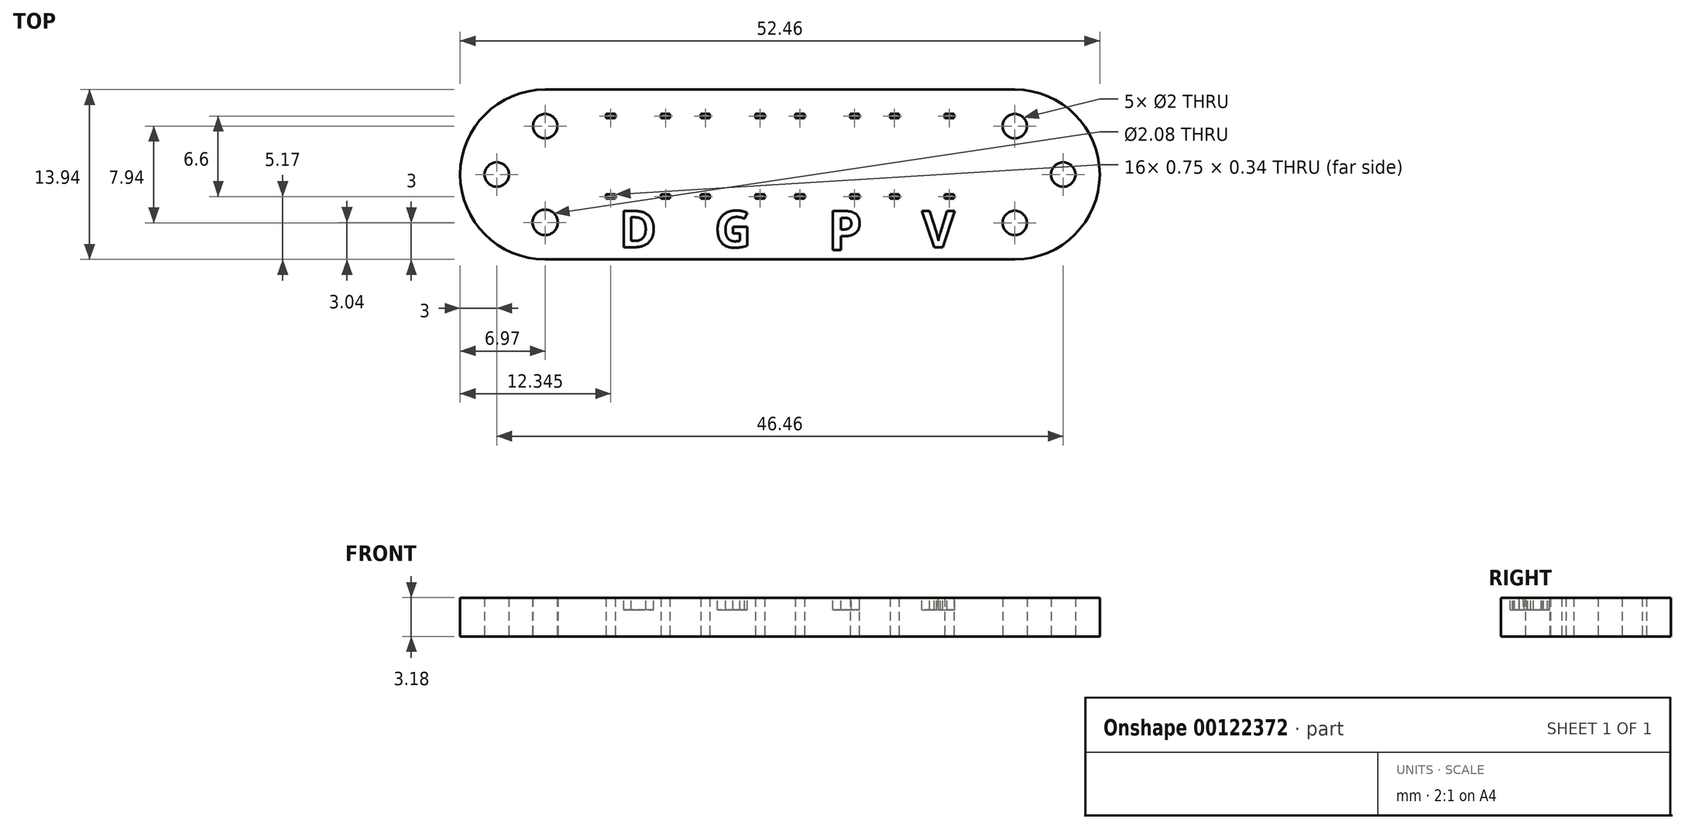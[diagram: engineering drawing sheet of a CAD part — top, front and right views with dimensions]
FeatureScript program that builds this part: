
annotation { "Feature Type Name" : "Feature", "Feature Type Description" : "" }
export const myFeature = defineFeature(function(context is Context, id is Id, definition is map)
    precondition{}
    {
        {
            var Q0;
            Q0=qCreatedBy(makeId("Top.planeOp"),FACE);
            var sketch = newSketch(context, id + "F0", { "sketchPlane" : qUnion([Q0])});
            skLineSegment(sketch, "E0.bottom", {"start": v(0, 0) * mm, "end": v(0.75, 0) * mm});
            skLineSegment(sketch, "E0.top", {"start": v(0, 0.34) * mm, "end": v(0.75, 0.34) * mm});
            skLineSegment(sketch, "E0.left", {"start": v(0, 0) * mm, "end": v(0, 0.34) * mm});
            skLineSegment(sketch, "E0.right", {"start": v(0.75, 0) * mm, "end": v(0.75, 0.34) * mm});
            skLineSegment(sketch, "E1.bottom", {"start": v(4.5, 0) * mm, "end": v(5.24, 0) * mm});
            skLineSegment(sketch, "E1.top", {"start": v(4.5, 0.34) * mm, "end": v(5.24, 0.34) * mm});
            skLineSegment(sketch, "E1.left", {"start": v(4.5, 0) * mm, "end": v(4.5, 0.34) * mm});
            skLineSegment(sketch, "E1.right", {"start": v(5.24, 0) * mm, "end": v(5.24, 0.34) * mm});
            skLineSegment(sketch, "E2.bottom", {"start": v(0, 6.94) * mm, "end": v(0.75, 6.94) * mm});
            skLineSegment(sketch, "E2.top", {"start": v(0, 6.6) * mm, "end": v(0.75, 6.6) * mm});
            skLineSegment(sketch, "E2.left", {"start": v(0, 6.94) * mm, "end": v(0, 6.6) * mm});
            skLineSegment(sketch, "E2.right", {"start": v(0.75, 6.94) * mm, "end": v(0.75, 6.6) * mm});
            skLineSegment(sketch, "E3.bottom", {"start": v(5.24, 6.94) * mm, "end": v(4.5, 6.94) * mm});
            skLineSegment(sketch, "E3.top", {"start": v(5.24, 6.6) * mm, "end": v(4.5, 6.6) * mm});
            skLineSegment(sketch, "E3.left", {"start": v(5.24, 6.94) * mm, "end": v(5.24, 6.6) * mm});
            skLineSegment(sketch, "E3.right", {"start": v(4.5, 6.94) * mm, "end": v(4.5, 6.6) * mm});
            skLineSegment(sketch, "E4", {"start": v(6.5, 0) * mm, "end": v(6.5, 8) * mm});
            skLineSegment(sketch, "E5.MirrorCS", {"start": v(7.76, 0) * mm, "end": v(7.76, 0.34) * mm});
            skLineSegment(sketch, "E6.MirrorCS", {"start": v(13, 6.94) * mm, "end": v(13, 6.6) * mm});
            skLineSegment(sketch, "E7.MirrorCS", {"start": v(12.25, 6.94) * mm, "end": v(12.25, 6.6) * mm});
            skLineSegment(sketch, "E8.MirrorCS", {"start": v(7.76, 6.94) * mm, "end": v(7.76, 6.6) * mm});
            skLineSegment(sketch, "E9.MirrorCS", {"start": v(8.5, 6.94) * mm, "end": v(8.5, 6.6) * mm});
            skLineSegment(sketch, "E10.MirrorCS", {"start": v(8.5, 0) * mm, "end": v(8.5, 0.34) * mm});
            skLineSegment(sketch, "E11.MirrorCS", {"start": v(13, 0) * mm, "end": v(13, 0.34) * mm});
            skLineSegment(sketch, "E12.MirrorCS", {"start": v(12.25, 0) * mm, "end": v(12.25, 0.34) * mm});
            skLineSegment(sketch, "E13.MirrorCS", {"start": v(13, 6.6) * mm, "end": v(12.25, 6.6) * mm});
            skLineSegment(sketch, "E14.MirrorCS", {"start": v(13, 6.94) * mm, "end": v(12.25, 6.94) * mm});
            skLineSegment(sketch, "E15.MirrorCS", {"start": v(7.76, 6.94) * mm, "end": v(8.5, 6.94) * mm});
            skLineSegment(sketch, "E16.MirrorCS", {"start": v(13, 0) * mm, "end": v(12.25, 0) * mm});
            skLineSegment(sketch, "E17.MirrorCS", {"start": v(13, 0.34) * mm, "end": v(12.25, 0.34) * mm});
            skLineSegment(sketch, "E18.MirrorCS", {"start": v(7.76, 6.6) * mm, "end": v(8.5, 6.6) * mm});
            skLineSegment(sketch, "E19.MirrorCS", {"start": v(8.5, 0) * mm, "end": v(7.76, 0) * mm});
            skLineSegment(sketch, "E20.MirrorCS", {"start": v(8.5, 0.34) * mm, "end": v(7.76, 0.34) * mm});
            skLineSegment(sketch, "E21", {"start": v(14.26, 0) * mm, "end": v(14.26, 8) * mm});
            skLineSegment(sketch, "E22.MirrorCS", {"start": v(15.52, 6.94) * mm, "end": v(15.52, 6.6) * mm});
            skLineSegment(sketch, "E23.MirrorCS", {"start": v(20.01, 0) * mm, "end": v(20.01, 0.34) * mm});
            skLineSegment(sketch, "E24.MirrorCS", {"start": v(20.76, 0) * mm, "end": v(20.76, 0.34) * mm});
            skLineSegment(sketch, "E25.MirrorCS", {"start": v(20.01, 6.94) * mm, "end": v(20.01, 6.6) * mm});
            skLineSegment(sketch, "E26.MirrorCS", {"start": v(16.27, 0) * mm, "end": v(16.27, 0.34) * mm});
            skLineSegment(sketch, "E27.MirrorCS", {"start": v(20.76, 6.94) * mm, "end": v(20.76, 6.6) * mm});
            skLineSegment(sketch, "E28.MirrorCS", {"start": v(16.27, 6.94) * mm, "end": v(16.27, 6.6) * mm});
            skLineSegment(sketch, "E29.MirrorCS", {"start": v(15.52, 0) * mm, "end": v(15.52, 0.34) * mm});
            skLineSegment(sketch, "E30.MirrorCS", {"start": v(20.01, 0) * mm, "end": v(20.76, 0) * mm});
            skLineSegment(sketch, "E31.MirrorCS", {"start": v(15.52, 6.6) * mm, "end": v(16.27, 6.6) * mm});
            skLineSegment(sketch, "E32.MirrorCS", {"start": v(20.76, 6.6) * mm, "end": v(20.01, 6.6) * mm});
            skLineSegment(sketch, "E33.MirrorCS", {"start": v(15.52, 0) * mm, "end": v(16.27, 0) * mm});
            skLineSegment(sketch, "E34.MirrorCS", {"start": v(20.01, 0.34) * mm, "end": v(20.76, 0.34) * mm});
            skLineSegment(sketch, "E35.MirrorCS", {"start": v(15.52, 0.34) * mm, "end": v(16.27, 0.34) * mm});
            skLineSegment(sketch, "E36.MirrorCS", {"start": v(20.76, 6.94) * mm, "end": v(20.01, 6.94) * mm});
            skLineSegment(sketch, "E37.MirrorCS", {"start": v(15.52, 6.94) * mm, "end": v(16.27, 6.94) * mm});
            skLineSegment(sketch, "E38.MirrorCS", {"start": v(28.52, 6.94) * mm, "end": v(28.52, 6.6) * mm});
            skLineSegment(sketch, "E39.MirrorCS", {"start": v(24.03, 6.94) * mm, "end": v(24.03, 6.6) * mm});
            skLineSegment(sketch, "E40.MirrorCS", {"start": v(23.28, 6.94) * mm, "end": v(23.28, 6.6) * mm});
            skLineSegment(sketch, "E41.MirrorCS", {"start": v(28.52, 0) * mm, "end": v(28.52, 0.34) * mm});
            skLineSegment(sketch, "E42.MirrorCS", {"start": v(27.77, 0) * mm, "end": v(27.77, 0.34) * mm});
            skLineSegment(sketch, "E43.MirrorCS", {"start": v(24.03, 0) * mm, "end": v(24.03, 0.34) * mm});
            skLineSegment(sketch, "E44.MirrorCS", {"start": v(23.28, 0) * mm, "end": v(23.28, 0.34) * mm});
            skLineSegment(sketch, "E45.MirrorCS", {"start": v(27.77, 6.94) * mm, "end": v(27.77, 6.6) * mm});
            skLineSegment(sketch, "E46.MirrorCS", {"start": v(23.28, 6.6) * mm, "end": v(24.03, 6.6) * mm});
            skLineSegment(sketch, "E47.MirrorCS", {"start": v(28.52, 0) * mm, "end": v(27.77, 0) * mm});
            skLineSegment(sketch, "E48.MirrorCS", {"start": v(28.52, 0.34) * mm, "end": v(27.77, 0.34) * mm});
            skLineSegment(sketch, "E49.MirrorCS", {"start": v(24.03, 0) * mm, "end": v(23.28, 0) * mm});
            skLineSegment(sketch, "E50.MirrorCS", {"start": v(24.03, 0.34) * mm, "end": v(23.28, 0.34) * mm});
            skLineSegment(sketch, "E51.MirrorCS", {"start": v(28.52, 6.6) * mm, "end": v(27.77, 6.6) * mm});
            skLineSegment(sketch, "E52.MirrorCS", {"start": v(28.52, 6.94) * mm, "end": v(27.77, 6.94) * mm});
            skLineSegment(sketch, "E53.MirrorCS", {"start": v(23.28, 6.94) * mm, "end": v(24.03, 6.94) * mm});
            skLineSegment(sketch, "E54.bottom", {"start": v(-5, 8.94) * mm, "end": v(33.52, 8.94) * mm});
            skLineSegment(sketch, "E54.top", {"start": v(-5, -5) * mm, "end": v(33.52, -5) * mm});
            skArc(sketch, "E55", {"start": v(33.52, -5) * mm, "mid": v(40.49, 1.97) * mm, "end": v(33.52, 8.94) * mm});
            skArc(sketch, "E56", {"start": v(-5, 8.94) * mm, "mid": v(-11.97, 1.97) * mm, "end": v(-5, -5) * mm});
            skCircle(sketch, "E57", {"center": v(33.52, 5.94) * mm, "radius": 1 * mm});
            skCircle(sketch, "E58", {"center": v(33.52, -2) * mm, "radius": 1 * mm});
            skCircle(sketch, "E59", {"center": v(37.49, 1.97) * mm, "radius": 1 * mm});
            skCircle(sketch, "E60", {"center": v(-8.97, 1.97) * mm, "radius": 1 * mm});
            skCircle(sketch, "E61", {"center": v(-5, 5.94) * mm, "radius": 1 * mm});
            skCircle(sketch, "E62", {"center": v(-5, -1.96) * mm, "radius": 1.04 * mm});
            skSolve(sketch);
        }
        {
            var Q0;
            Q0=makeQuery(id+"F0.imprint","IMPRINT",FACE,{"disambiguationData":[TD([[makeQuery(id+"F0.imprint","IMPRINT",EDGE,{"derivedFrom":sQuery(id+"F0.wireOp",EDGE,"E0.bottom")}),-1.0]])]});
            extrude(context, id + "F1", {"entities" : qUnion([Q0]), "depth" : 3.17 * mm});
        }
        {
            var Q0;
            Q0=makeQuery(id+"F1.opExtrude","CAP_FACE",FACE,{"disambiguationData":[OSD([sQuery(id+"F0.wireOp",EDGE,"E0.bottom"),sQuery(id+"F0.wireOp",EDGE,"E0.top"),sQuery(id+"F0.wireOp",EDGE,"E0.left"),sQuery(id+"F0.wireOp",EDGE,"E0.right"),sQuery(id+"F0.wireOp",EDGE,"E1.bottom"),sQuery(id+"F0.wireOp",EDGE,"E1.top"),sQuery(id+"F0.wireOp",EDGE,"E1.left"),sQuery(id+"F0.wireOp",EDGE,"E1.right"),sQuery(id+"F0.wireOp",EDGE,"E2.bottom"),sQuery(id+"F0.wireOp",EDGE,"E2.top"),sQuery(id+"F0.wireOp",EDGE,"E2.left"),sQuery(id+"F0.wireOp",EDGE,"E2.right"),sQuery(id+"F0.wireOp",EDGE,"E3.bottom"),sQuery(id+"F0.wireOp",EDGE,"E3.top"),sQuery(id+"F0.wireOp",EDGE,"E3.left"),sQuery(id+"F0.wireOp",EDGE,"E3.right"),sQuery(id+"F0.wireOp",EDGE,"E5.MirrorCS"),sQuery(id+"F0.wireOp",EDGE,"E6.MirrorCS"),sQuery(id+"F0.wireOp",EDGE,"E7.MirrorCS"),sQuery(id+"F0.wireOp",EDGE,"E8.MirrorCS"),sQuery(id+"F0.wireOp",EDGE,"E9.MirrorCS"),sQuery(id+"F0.wireOp",EDGE,"E10.MirrorCS"),sQuery(id+"F0.wireOp",EDGE,"E11.MirrorCS"),sQuery(id+"F0.wireOp",EDGE,"E12.MirrorCS"),sQuery(id+"F0.wireOp",EDGE,"E13.MirrorCS"),sQuery(id+"F0.wireOp",EDGE,"E14.MirrorCS"),sQuery(id+"F0.wireOp",EDGE,"E15.MirrorCS"),sQuery(id+"F0.wireOp",EDGE,"E16.MirrorCS"),sQuery(id+"F0.wireOp",EDGE,"E17.MirrorCS"),sQuery(id+"F0.wireOp",EDGE,"E18.MirrorCS"),sQuery(id+"F0.wireOp",EDGE,"E19.MirrorCS"),sQuery(id+"F0.wireOp",EDGE,"E20.MirrorCS"),sQuery(id+"F0.wireOp",EDGE,"E22.MirrorCS"),sQuery(id+"F0.wireOp",EDGE,"E23.MirrorCS"),sQuery(id+"F0.wireOp",EDGE,"E24.MirrorCS"),sQuery(id+"F0.wireOp",EDGE,"E25.MirrorCS"),sQuery(id+"F0.wireOp",EDGE,"E26.MirrorCS"),sQuery(id+"F0.wireOp",EDGE,"E27.MirrorCS"),sQuery(id+"F0.wireOp",EDGE,"E28.MirrorCS"),sQuery(id+"F0.wireOp",EDGE,"E29.MirrorCS"),sQuery(id+"F0.wireOp",EDGE,"E30.MirrorCS"),sQuery(id+"F0.wireOp",EDGE,"E31.MirrorCS"),sQuery(id+"F0.wireOp",EDGE,"E32.MirrorCS"),sQuery(id+"F0.wireOp",EDGE,"E33.MirrorCS"),sQuery(id+"F0.wireOp",EDGE,"E34.MirrorCS"),sQuery(id+"F0.wireOp",EDGE,"E35.MirrorCS"),sQuery(id+"F0.wireOp",EDGE,"E36.MirrorCS"),sQuery(id+"F0.wireOp",EDGE,"E37.MirrorCS"),sQuery(id+"F0.wireOp",EDGE,"E38.MirrorCS"),sQuery(id+"F0.wireOp",EDGE,"E39.MirrorCS"),sQuery(id+"F0.wireOp",EDGE,"E40.MirrorCS"),sQuery(id+"F0.wireOp",EDGE,"E41.MirrorCS"),sQuery(id+"F0.wireOp",EDGE,"E42.MirrorCS"),sQuery(id+"F0.wireOp",EDGE,"E43.MirrorCS"),sQuery(id+"F0.wireOp",EDGE,"E44.MirrorCS"),sQuery(id+"F0.wireOp",EDGE,"E45.MirrorCS"),sQuery(id+"F0.wireOp",EDGE,"E46.MirrorCS"),sQuery(id+"F0.wireOp",EDGE,"E47.MirrorCS"),sQuery(id+"F0.wireOp",EDGE,"E48.MirrorCS"),sQuery(id+"F0.wireOp",EDGE,"E49.MirrorCS"),sQuery(id+"F0.wireOp",EDGE,"E50.MirrorCS"),sQuery(id+"F0.wireOp",EDGE,"E51.MirrorCS"),sQuery(id+"F0.wireOp",EDGE,"E52.MirrorCS"),sQuery(id+"F0.wireOp",EDGE,"E53.MirrorCS"),sQuery(id+"F0.wireOp",EDGE,"E54.bottom"),sQuery(id+"F0.wireOp",EDGE,"E54.top"),sQuery(id+"F0.wireOp",EDGE,"E55"),sQuery(id+"F0.wireOp",EDGE,"E56"),sQuery(id+"F0.wireOp",EDGE,"E57"),sQuery(id+"F0.wireOp",EDGE,"E58"),sQuery(id+"F0.wireOp",EDGE,"E59"),sQuery(id+"F0.wireOp",EDGE,"E60"),sQuery(id+"F0.wireOp",EDGE,"E61"),sQuery(id+"F0.wireOp",EDGE,"E62")])],"isStart":false});
            var sketch = newSketch(context, id + "F2", { "sketchPlane" : qUnion([Q0])});
            skText(sketch, "E63", { "text": "G", "fontName": "OpenSans-Bold.ttf"});
            skText(sketch, "E64", { "text": "D", "fontName": "OpenSans-Bold.ttf"});
            skText(sketch, "E65", { "text": "P", "fontName": "OpenSans-Bold.ttf"});
            skText(sketch, "E66", { "text": "V", "fontName": "OpenSans-Bold.ttf"});
            skLineSegment(sketch, "E67", {"start": v(0.75, 0) * mm, "end": v(4.5, 0) * mm});
            skLineSegment(sketch, "E68", {"start": v(0, 0) * mm, "end": v(0, -5) * mm});
            const initialGuessF2  = {"E63": [0.0089, -0.004, 1, 0, 0.003], "E64": [0.00106, -0.004, 1, 0, 0.003], "E65": [0.01818, -0.00423, 1, 0, 0.00323], "E66": [0.0259, -0.004, 1, 0, 0.003]};
            skSetInitialGuess(sketch, initialGuessF2);
            skSolve(sketch);
        }
        {
            var Q0;
            Q0 = qSketchRegion(id + "F2", true);
            extrude(context, id + "F3", {"entities" : qUnion([Q0]), "operationType" : NewBodyOperationType.REMOVE, "oppositeDirection" : true, "depth" : 1 * mm});
        }
    });
